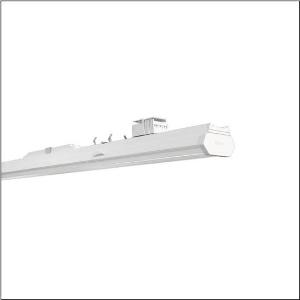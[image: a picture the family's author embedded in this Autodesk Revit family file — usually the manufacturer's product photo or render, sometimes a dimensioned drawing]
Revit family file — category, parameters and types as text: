
# Revit family: licross_r__11_protected_mo_51td117n485g_c933
name_source: partatom
category: Lighting Fixtures
units: mm (PartAtom-declared; Revit-internal decimal feet)

## family parameters
Cut with Voids When Loaded = No
Host = Face
Light Source = No
Part Type = Normal
Room Calculation Point = No
Round Connector Dimension = Use Diameter
Shared = No

## types (1)
- Licross® 11 Protected MO (1 x LED, 8680 lm, 48.6 W, 4000K)
    Apparent Load = 49 VA
    CIE Flux Codes = 83 94 98 100 100
    Color Rendering = 80
    Color Temperature = 4000K
    Default Elevation = 1800 mm
    Description = Licross® 11 Protected MO, luminaire insert, of sheet steel, galvanised, coil coated, white, length: 1.500mm, width: 90mm, height: 101mm, LED rated luminous flux: 8.680lm, light colour: 840, control gear: ON/OFF, with plug, 3-pole, with phase selection, mains connection: 220..240V, AC, 50/60Hz, rated input power: 49W, halogen-free wiring, primary light control with lens, of plastic, primary optical cover: cover, of PMMA, light emission: direct distribution, primary light characteristic: symmetric, protection rating (complete): IP54, insulation class (complete): insulation class I (protective earthing), certification: CE, ENEC, VDE, UKCA, protection symbol: D if used in an environment with non-conductive dust loads with corresponding accessories, impact resistance: IK06, permissible ambient temperature for indoor applications: -25..+35°C, corresponds to IFS (International Featured Standards) requirements for safety and quality in the food industry, reducing of maximum allowable ambient temperature of 5°C with ceiling mounting, LABS conformity tested according to VDMA 24364:2018-05, packaging unit: 1 piece
    Height = 92 mm
    Lamp = 1 x LED
    Lamp Light Flux = 8680 lm
    Lamp Power = 48.6 W
    Lamp count = 1
    Length = 1500 mm
    Luminous efficacy = 179 lm/W
    Manufacturer = Siteco
    ModVariant = No
    Model = 51TD117N485G
    Mounting Place = Ceiling
    Mounting Type = Pendant
    Number of Poles = 1
    OnlyDefault = Yes
    Power Factor = 1
    Product Name = Licross® 11 Protected MO
    Product group = luminaire insert
    ProductGroupID = 901
    Protection Class = Protection class I
    Protection Degree = IP 54
    RLX_Detail_Level = 1
    RLX_Emergency_Light_Flux = 0 lm
    RLX_Emergency_Type = 0
    RLX_Emergency_Type_DB = No
    RlxData = <blob elided: 20369 chars, md5=20df8300>
    Socket = socket
    Standby Power = 0 W
    System Light Flux = 8680 lm
    System Power = 49 W
    Type Comments = Product without accessories
    Type Image = l_1256145.jpg
    URL = http://relux.com
    VarID = ---
    Voltage = 0 V
    Weight = 0.00 kg
    Width = 88 mm

## geometry (parser evidence)
native form markers: Blend x4, Sweep x9
no freeform markers — native parametric forms only
